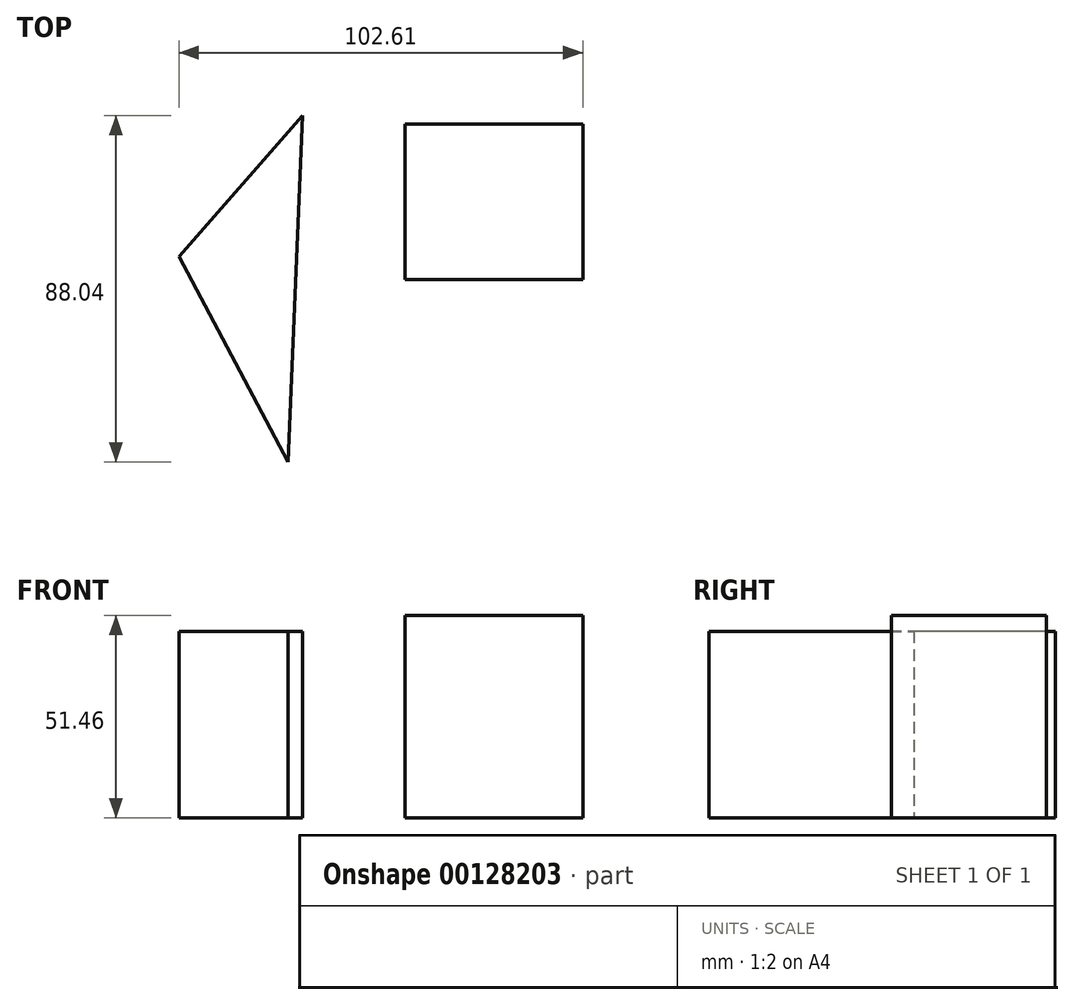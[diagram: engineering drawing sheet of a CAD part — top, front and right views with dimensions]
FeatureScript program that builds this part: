
annotation { "Feature Type Name" : "Feature", "Feature Type Description" : "" }
export const myFeature = defineFeature(function(context is Context, id is Id, definition is map)
    precondition{}
    {
        {
            var Q0;
            Q0=qCreatedBy(makeId("Top.planeOp"),FACE);
            var sketch = newSketch(context, id + "F0", { "sketchPlane" : qUnion([Q0])});
            skLineSegment(sketch, "E0.bottom", {"start": v(0, 39.38) * mm, "end": v(45.15, 39.38) * mm});
            skLineSegment(sketch, "E0.top", {"start": v(0, 0) * mm, "end": v(45.15, 0) * mm});
            skLineSegment(sketch, "E0.left", {"start": v(0, 39.38) * mm, "end": v(0, 0) * mm});
            skLineSegment(sketch, "E0.right", {"start": v(45.15, 39.38) * mm, "end": v(45.15, 0) * mm});
            skSolve(sketch);
        }
        {
            var Q0;
            Q0 = qSketchRegion(id + "F0", true);
            extrude(context, id + "F1", {"entities" : qUnion([Q0]), "depth" : 51.46 * mm});
        }
        {
            var Q0;
            Q0=qCreatedBy(makeId("Top.planeOp"),FACE);
            var sketch = newSketch(context, id + "F2", { "sketchPlane" : qUnion([Q0])});
            skLineSegment(sketch, "E1", {"start": v(-26.07, 41.63) * mm, "end": v(-57.46, 5.73) * mm});
            skLineSegment(sketch, "E2", {"start": v(-29.68, -46.41) * mm, "end": v(-57.46, 5.73) * mm});
            skLineSegment(sketch, "E3", {"start": v(-26.07, 41.63) * mm, "end": v(-29.68, -46.41) * mm});
            skSolve(sketch);
        }
        {
            var Q0;
            Q0 = qSketchRegion(id + "F2", true);
            extrude(context, id + "F3", {"entities" : qUnion([Q0]), "depth" : 47.46 * mm});
        }
    });
